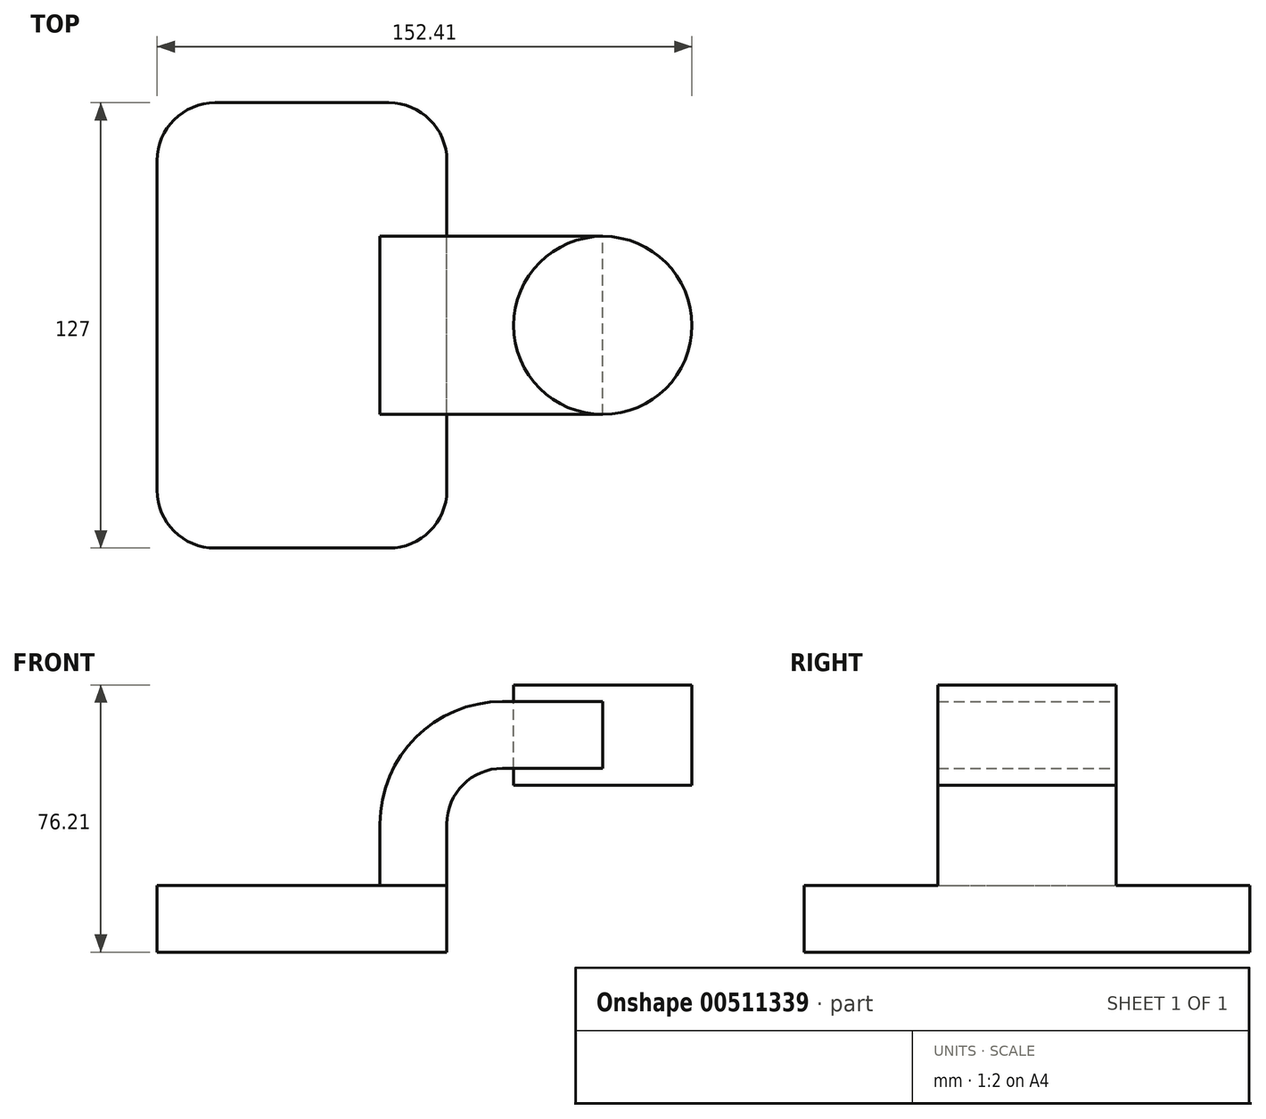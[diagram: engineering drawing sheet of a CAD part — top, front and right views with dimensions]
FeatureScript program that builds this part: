
annotation { "Feature Type Name" : "Feature", "Feature Type Description" : "" }
export const myFeature = defineFeature(function(context is Context, id is Id, definition is map)
    precondition{}
    {
        {
            var Q0;
            Q0=qCreatedBy(makeId("Front.planeOp"),FACE);
            var sketch = newSketch(context, id + "F0", { "sketchPlane" : qUnion([Q0])});
            skLineSegment(sketch, "E0.bottom", {"start": v(-41.27, 9.52) * mm, "end": v(41.28, 9.52) * mm});
            skLineSegment(sketch, "E0.top", {"start": v(-41.27, -9.53) * mm, "end": v(41.28, -9.53) * mm});
            skLineSegment(sketch, "E0.left", {"start": v(-41.28, 9.52) * mm, "end": v(-41.28, -9.52) * mm});
            skLineSegment(sketch, "E0.right", {"start": v(41.28, 9.52) * mm, "end": v(41.28, -9.52) * mm});
            skPoint(sketch, "E0.middle", {"position": v(0, 0) * mm});
            skLineSegment(sketch, "E1.bottom", {"start": v(111.13, 38.1) * mm, "end": v(60.33, 38.1) * mm});
            skLineSegment(sketch, "E1.top", {"start": v(111.13, 66.67) * mm, "end": v(60.33, 66.67) * mm});
            skLineSegment(sketch, "E1.left", {"start": v(111.13, 38.1) * mm, "end": v(111.13, 66.68) * mm});
            skLineSegment(sketch, "E1.right", {"start": v(60.33, 38.1) * mm, "end": v(60.33, 66.68) * mm});
            skPoint(sketch, "E1.middle", {"position": v(85.73, 52.39) * mm});
            skLineSegment(sketch, "E2", {"start": v(41.28, 9.52) * mm, "end": v(41.28, 27) * mm});
            skArc(sketch, "E3", {"start": v(41.28, 27) * mm, "mid": v(45.92, 38.23) * mm, "end": v(57.15, 42.88) * mm});
            skLineSegment(sketch, "E4", {"start": v(57.15, 42.88) * mm, "end": v(85.73, 42.88) * mm});
            skLineSegment(sketch, "E5.0", {"start": v(57.15, 61.93) * mm, "end": v(85.73, 61.93) * mm});
            skArc(sketch, "E5.1", {"start": v(22.23, 27) * mm, "mid": v(32.45, 51.7) * mm, "end": v(57.15, 61.93) * mm});
            skLineSegment(sketch, "E5.2", {"start": v(22.23, 9.52) * mm, "end": v(22.23, 27) * mm});
            skFitSpline(sketch, "E6", {"points": [v(57.15, 61.93) * mm, v(-41.28, 9.52) * mm], "startDerivative": vector(-109.33, 0) * mm, "endDerivative": vector(0, -72.62) * mm});
            skLineSegment(sketch, "E7", {"start": v(85.73, 66.67) * mm, "end": v(85.73, 38.1) * mm});
            skSolve(sketch);
        }
        {
            var Q0;
            Q0=makeQuery(id+"F0.imprint","IMPRINT",FACE,{"disambiguationData":[TD([[makeQuery(id+"F0.imprint","IMPRINT",EDGE,{"derivedFrom":sQuery(id+"F0.wireOp",EDGE,"E0.top")}),1.0]])]});
            extrude(context, id + "F1", {"entities" : qUnion([Q0]), "endBound" : BoundingType.SYMMETRIC, "depth" : 127 * mm});
        }
        {
            var Q0;
            {var subQ1=sQuery(id+"F0.wireOp",EDGE,"E2");Q0=makeQuery(id+"F0.imprint","IMPRINT",FACE,{"disambiguationData":[TD([[makeQuery(id+"F0.imprint","IMPRINT",EDGE,{"derivedFrom":subQ1}),1.0]])]});}
            var Q1;
            {var subQ0=sQuery(id+"F0.wireOp",EDGE,"E4");var subQ1=sQuery(id+"F0.wireOp",EDGE,"E1.right");var subQ2=makeQuery(id+"F0.imprint","INTERSECT",VERTEX,{"derivedFrom":[subQ1,subQ0]});Q1=makeQuery(id+"F0.imprint","IMPRINT",FACE,{"disambiguationData":[TD([[makeQuery(id+"F0.imprint","IMPRINT",EDGE,{"disambiguationData":[TD([[subQ2,-1.0]])],"derivedFrom":subQ1}),-1.0]])]});}
            extrude(context, id + "F2", {"entities" : qUnion([Q0, Q1]), "operationType" : NewBodyOperationType.ADD, "endBound" : BoundingType.SYMMETRIC, "depth" : 50.8 * mm});
        }
        {
            var Q0;
            Q0=makeQuery(id+"F0.imprint","IMPRINT",FACE,{"disambiguationData":[TD([[makeQuery(id+"F0.imprint","IMPRINT",EDGE,{"derivedFrom":sQuery(id+"F0.wireOp",EDGE,"E5.1")}),1.0]])]});
            extrude(context, id + "F3", {"entities" : qUnion([Q0]), "operationType" : NewBodyOperationType.ADD, "endBound" : BoundingType.SYMMETRIC, "depth" : 15.88 * mm});
        }
        {
            var Q0;
            {var subQ0=sQuery(id+"F0.wireOp",EDGE,"E1.left");Q0=makeQuery(id+"F0.imprint","IMPRINT",FACE,{"disambiguationData":[TD([[makeQuery(id+"F0.imprint","IMPRINT",EDGE,{"derivedFrom":subQ0}),1.0]])]});}
            var Q1;
            Q1=sQuery(id+"F0.wireOp",EDGE,"E7");
            revolve(context, id + "F4", {"entities" : qUnion([Q0]), "axis" : qUnion([Q1]), "revolveType" : RevolveType.FULL});
        }
        {
            var Q0;
            Q0=makeQuery(id+"F1.opExtrude","CAP_EDGE",EDGE,{"disambiguationData":[OSD([sQuery(id+"F0.wireOp",EDGE,"E0.left")])],"isStart":false});
            var Q1;
            Q1=makeQuery(id+"F1.opExtrude","CAP_EDGE",EDGE,{"disambiguationData":[OSD([sQuery(id+"F0.wireOp",EDGE,"E0.right")])],"isStart":false});
            var Q2;
            Q2=makeQuery(id+"F1.opExtrude","CAP_EDGE",EDGE,{"disambiguationData":[OSD([sQuery(id+"F0.wireOp",EDGE,"E0.right")])],"isStart":true});
            var Q3;
            Q3=makeQuery(id+"F1.opExtrude","CAP_EDGE",EDGE,{"disambiguationData":[OSD([sQuery(id+"F0.wireOp",EDGE,"E0.left")])],"isStart":true});
            fillet(context, id + "F5", {"entities" : qUnion([Q0, Q1, Q2, Q3]), "radius" : 16.5 * mm, "tangentPropagation" : true, "allowEdgeOverflow" : false});
        }
    });
